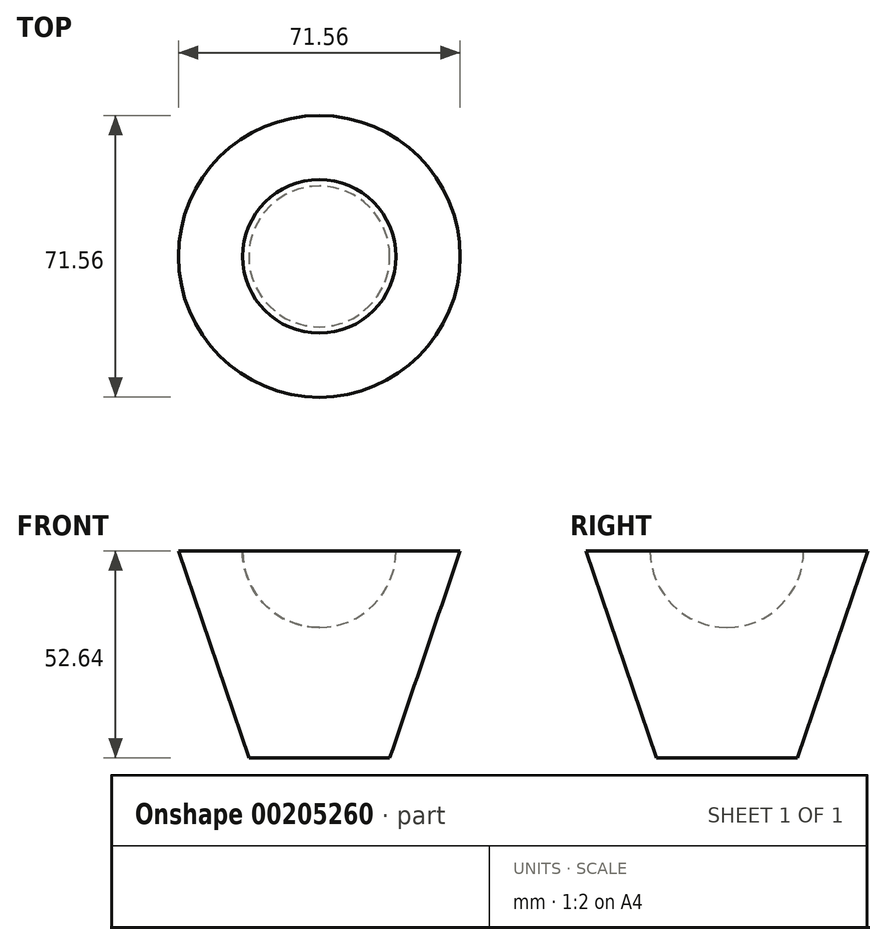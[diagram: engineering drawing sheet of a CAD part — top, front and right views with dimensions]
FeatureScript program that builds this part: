
annotation { "Feature Type Name" : "Feature", "Feature Type Description" : "" }
export const myFeature = defineFeature(function(context is Context, id is Id, definition is map)
    precondition{}
    {
        {
            var Q0;
            Q0=qCreatedBy(makeId("Front.planeOp"),FACE);
            var sketch = newSketch(context, id + "F0", { "sketchPlane" : qUnion([Q0])});
            skLineSegment(sketch, "E0", {"start": v(0, 0) * mm, "end": v(0, -52.64) * mm});
            skLineSegment(sketch, "E1", {"start": v(0, -52.64) * mm, "end": v(-17.9, -52.64) * mm});
            skLineSegment(sketch, "E2", {"start": v(-17.9, -52.64) * mm, "end": v(-35.78, 0) * mm});
            skLineSegment(sketch, "E3", {"start": v(-35.78, 0) * mm, "end": v(-19.26, 0) * mm});
            skArc(sketch, "E4", {"start": v(-19.5, 0) * mm, "mid": v(-13.78, -13.78) * mm, "end": v(0, -19.5) * mm});
            skArc(sketch, "E5", {"start": v(0, -19.5) * mm, "mid": v(13.78, 13.78) * mm, "end": v(-19.5, 0) * mm, "construction": true});
            skSolve(sketch);
        }
        {
            var Q0;
            {var subQ3=sQuery(id+"F0.wireOp",EDGE,"E1");Q0=makeQuery(id+"F0.imprint","IMPRINT",FACE,{"disambiguationData":[TD([[makeQuery(id+"F0.imprint","IMPRINT",EDGE,{"derivedFrom":subQ3}),-1.0]])]});}
            var Q1;
            Q1=sQuery(id+"F0.wireOp",EDGE,"E0");
            revolve(context, id + "F1", {"entities" : qUnion([Q0]), "axis" : qUnion([Q1]), "revolveType" : RevolveType.FULL});
        }
    });
